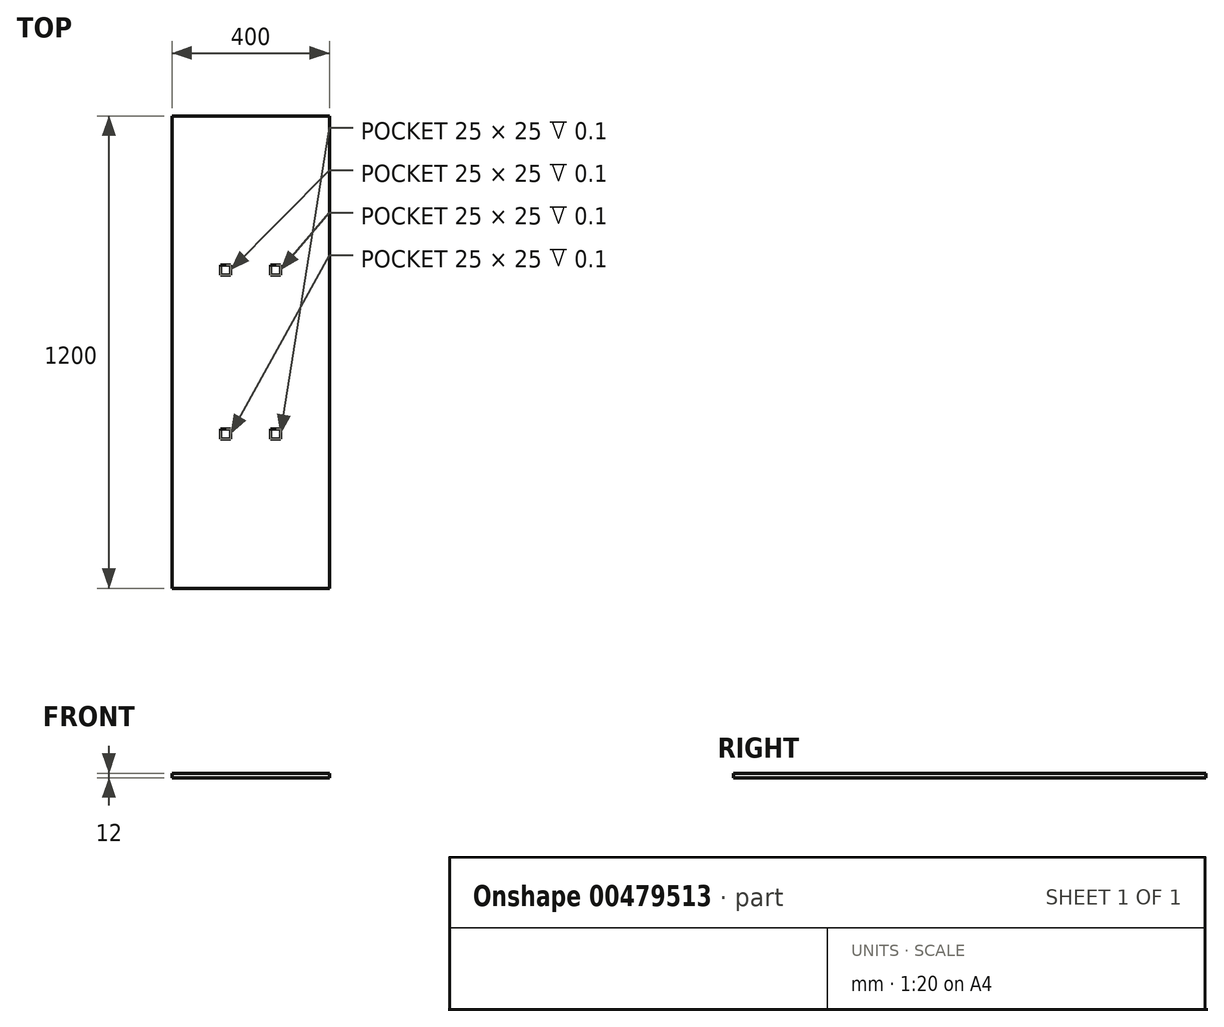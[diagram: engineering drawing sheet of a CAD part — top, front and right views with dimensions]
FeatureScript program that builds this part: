
annotation { "Feature Type Name" : "Feature", "Feature Type Description" : "" }
export const myFeature = defineFeature(function(context is Context, id is Id, definition is map)
    precondition{}
    {
        {
            var Q0;
            Q0=qCreatedBy(makeId("Top.planeOp"),FACE);
            var sketch = newSketch(context, id + "F0", { "sketchPlane" : qUnion([Q0])});
            skLineSegment(sketch, "E0.bottom", {"start": v(383.48, 1032.2) * mm, "end": v(-16.52, 1032.2) * mm});
            skLineSegment(sketch, "E0.top", {"start": v(383.48, -167.8) * mm, "end": v(-16.52, -167.8) * mm});
            skLineSegment(sketch, "E0.left", {"start": v(383.48, 1032.2) * mm, "end": v(383.48, -167.8) * mm});
            skLineSegment(sketch, "E0.right", {"start": v(-16.52, 1032.2) * mm, "end": v(-16.52, -167.8) * mm});
            skSolve(sketch);
        }
        {
            var Q0;
            Q0=makeQuery(id+"F0.imprint","IMPRINT",FACE,{"disambiguationData":[TD([[makeQuery(id+"F0.imprint","IMPRINT",EDGE,{"derivedFrom":sQuery(id+"F0.wireOp",EDGE,"E0.bottom")}),1.0]])]});
            extrude(context, id + "F1", {"entities" : qUnion([Q0]), "depth" : 12 * mm});
        }
        {
            var Q0;
            Q0=makeQuery(id+"F1.opExtrude","CAP_FACE",FACE,{"disambiguationData":[OSD([sQuery(id+"F0.wireOp",EDGE,"E0.bottom"),sQuery(id+"F0.wireOp",EDGE,"E0.top"),sQuery(id+"F0.wireOp",EDGE,"E0.left"),sQuery(id+"F0.wireOp",EDGE,"E0.right")])],"isStart":false});
            var sketch = newSketch(context, id + "F2", { "sketchPlane" : qUnion([Q0])});
            skLineSegment(sketch, "E1", {"start": v(383.48, -167.8) * mm, "end": v(383.48, 132.2) * mm, "construction": true});
            skLineSegment(sketch, "E2.bottom", {"start": v(259.68, 236.21) * mm, "end": v(234.68, 236.21) * mm});
            skLineSegment(sketch, "E2.top", {"start": v(259.68, 211.21) * mm, "end": v(234.68, 211.21) * mm});
            skLineSegment(sketch, "E2.left", {"start": v(259.68, 236.21) * mm, "end": v(259.68, 211.21) * mm});
            skLineSegment(sketch, "E2.right", {"start": v(234.68, 236.21) * mm, "end": v(234.68, 211.21) * mm});
            skPoint(sketch, "E2.middle", {"position": v(247.18, 223.71) * mm});
            skLineSegment(sketch, "E3", {"start": v(183.48, -167.8) * mm, "end": v(183.48, 1032.2) * mm, "construction": true});
            skLineSegment(sketch, "E4", {"start": v(-16.52, 432.2) * mm, "end": v(383.48, 432.2) * mm, "construction": true});
            skLineSegment(sketch, "E5.MirrorCS", {"start": v(132.28, 236.21) * mm, "end": v(132.28, 211.21) * mm});
            skLineSegment(sketch, "E6.MirrorCS", {"start": v(107.28, 236.21) * mm, "end": v(132.28, 236.21) * mm});
            skLineSegment(sketch, "E7.MirrorCS", {"start": v(107.28, 236.21) * mm, "end": v(107.28, 211.21) * mm});
            skLineSegment(sketch, "E8.MirrorCS", {"start": v(107.28, 211.21) * mm, "end": v(132.28, 211.21) * mm});
            skLineSegment(sketch, "E9.MirrorCS", {"start": v(259.68, 628.17) * mm, "end": v(234.68, 628.17) * mm});
            skLineSegment(sketch, "E10.MirrorCS", {"start": v(234.68, 628.17) * mm, "end": v(234.68, 653.17) * mm});
            skLineSegment(sketch, "E11.MirrorCS", {"start": v(259.68, 628.17) * mm, "end": v(259.68, 653.17) * mm});
            skLineSegment(sketch, "E12.MirrorCS", {"start": v(259.68, 653.17) * mm, "end": v(234.68, 653.17) * mm});
            skLineSegment(sketch, "E13.MirrorCS", {"start": v(107.28, 653.17) * mm, "end": v(132.28, 653.17) * mm});
            skLineSegment(sketch, "E14.MirrorCS", {"start": v(132.28, 628.17) * mm, "end": v(132.28, 653.17) * mm});
            skLineSegment(sketch, "E15.MirrorCS", {"start": v(107.28, 628.17) * mm, "end": v(132.28, 628.17) * mm});
            skLineSegment(sketch, "E16.MirrorCS", {"start": v(107.28, 628.17) * mm, "end": v(107.28, 653.17) * mm});
            skLineSegment(sketch, "E17", {"start": v(247.18, 211.21) * mm, "end": v(247.18, 653.17) * mm, "construction": true});
            skLineSegment(sketch, "E18", {"start": v(107.28, 223.71) * mm, "end": v(259.68, 223.71) * mm, "construction": true});
            skSolve(sketch);
        }
        {
            var Q0;
            Q0 = qSketchRegion(id + "F2", true);
            extrude(context, id + "F3", {"entities" : qUnion([Q0]), "operationType" : NewBodyOperationType.REMOVE, "oppositeDirection" : true, "depth" : .1 * mm});
        }
    });
